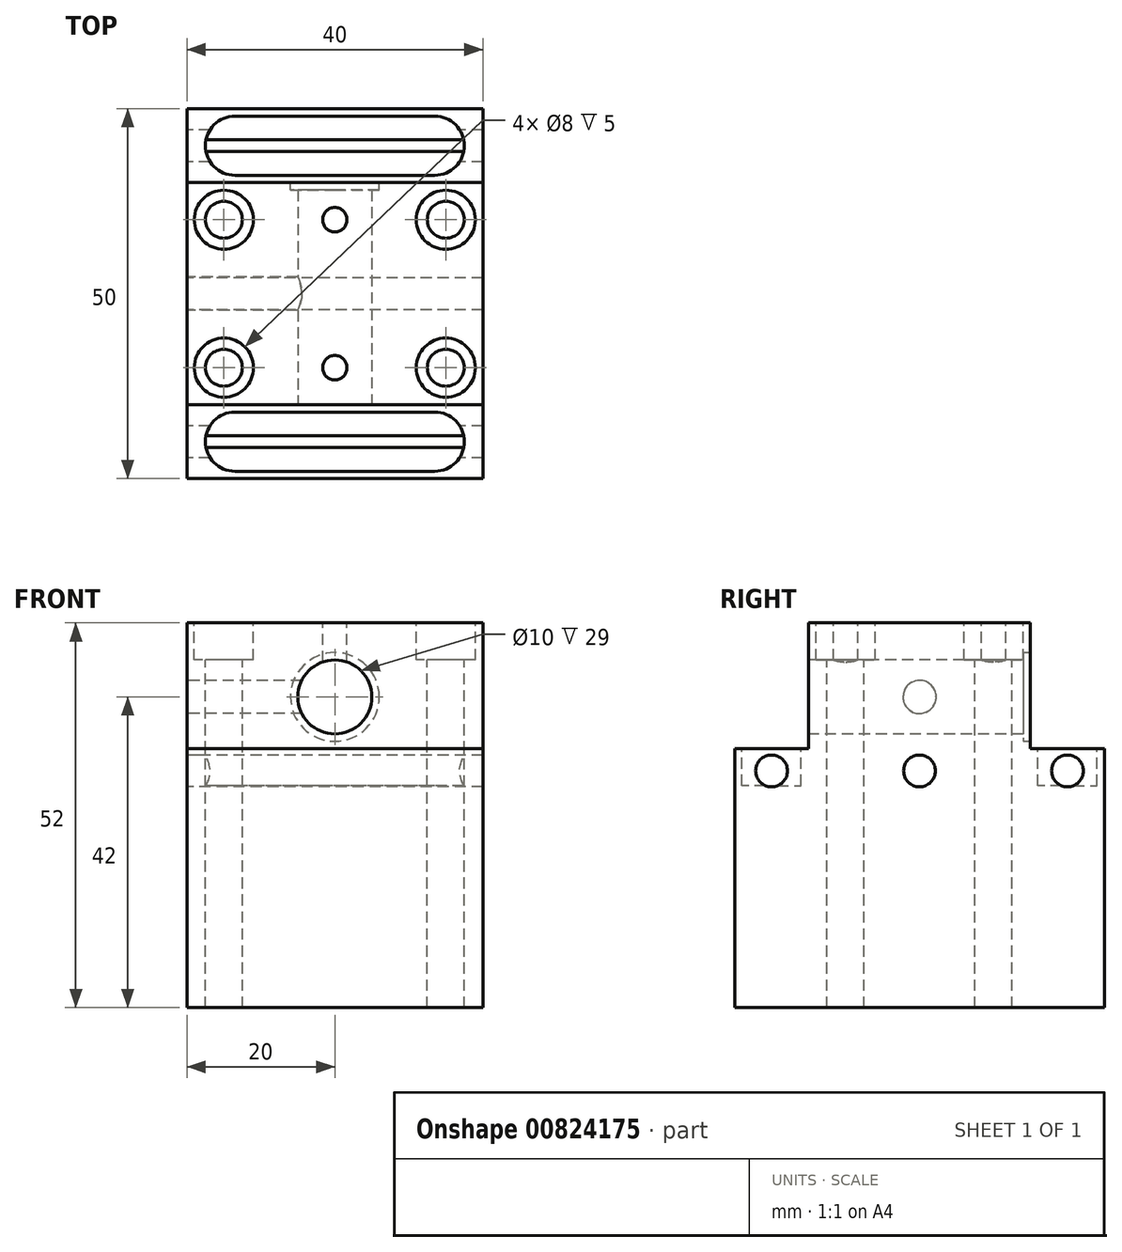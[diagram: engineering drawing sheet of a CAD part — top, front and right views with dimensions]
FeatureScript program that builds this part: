
annotation { "Feature Type Name" : "Feature", "Feature Type Description" : "" }
export const myFeature = defineFeature(function(context is Context, id is Id, definition is map)
    precondition{}
    {
        {
            var Q0;
            Q0=qCreatedBy(makeId("Top.planeOp"),FACE);
            var sketch = newSketch(context, id + "F0", { "sketchPlane" : qUnion([Q0])});
            skLineSegment(sketch, "E0.bottom", {"start": v(0, 0) * mm, "end": v(40, 0) * mm});
            skLineSegment(sketch, "E0.top", {"start": v(0, 30) * mm, "end": v(40, 30) * mm});
            skLineSegment(sketch, "E0.left", {"start": v(0, 0) * mm, "end": v(0, 30) * mm});
            skLineSegment(sketch, "E0.right", {"start": v(40, 0) * mm, "end": v(40, 30) * mm});
            skSolve(sketch);
        }
        {
            var Q0;
            Q0 = qSketchRegion(id + "F0", true);
            extrude(context, id + "F1", {"entities" : qUnion([Q0]), "depth" : 52 * mm, "offsetDistance" : 25 * mm});
        }
        {
            var Q0;
            Q0=makeQuery(id+"F1.opExtrude","SWEPT_FACE",FACE,{"disambiguationData":[OSD([sQuery(id+"F0.wireOp",EDGE,"E0.bottom")])]});
            var sketch = newSketch(context, id + "F2", { "sketchPlane" : qUnion([Q0])});
            skLineSegment(sketch, "E1", {"start": v(0, 42) * mm, "end": v(40, 42) * mm, "construction": true});
            skCircle(sketch, "E2", {"center": v(20, 42) * mm, "radius": 5 * mm});
            skSolve(sketch);
        }
        {
            var Q0;
            Q0 = qSketchRegion(id + "F2", true);
            extrude(context, id + "F3", {"entities" : qUnion([Q0]), "operationType" : NewBodyOperationType.REMOVE, "oppositeDirection" : true, "depth" : 20 * mm, "offsetDistance" : 25 * mm});
        }
        {
            var Q0;
            Q0=makeQuery(id+"F1.opExtrude","CAP_FACE",FACE,{"disambiguationData":[OSD([sQuery(id+"F0.wireOp",EDGE,"E0.bottom"),sQuery(id+"F0.wireOp",EDGE,"E0.top"),sQuery(id+"F0.wireOp",EDGE,"E0.left"),sQuery(id+"F0.wireOp",EDGE,"E0.right")])],"isStart":false});
            var sketch = newSketch(context, id + "F4", { "sketchPlane" : qUnion([Q0])});
            skLineSegment(sketch, "E3", {"start": v(0, 5) * mm, "end": v(40, 5) * mm, "construction": true});
            skLineSegment(sketch, "E4", {"start": v(0, 25) * mm, "end": v(40, 25) * mm, "construction": true});
            skCircle(sketch, "E5", {"center": v(20, 5) * mm, "radius": 1.65 * mm});
            skCircle(sketch, "E6", {"center": v(20, 25) * mm, "radius": 1.65 * mm});
            skLineSegment(sketch, "E7", {"start": v(0, 15) * mm, "end": v(40, 15) * mm, "construction": true});
            skSolve(sketch);
        }
        {
            var Q0;
            Q0 = qSketchRegion(id + "F4", true);
            extrude(context, id + "F5", {"entities" : qUnion([Q0]), "operationType" : NewBodyOperationType.REMOVE, "oppositeDirection" : true, "depth" : 10 * mm, "offsetDistance" : 25 * mm});
        }
        {
            var Q0;
            Q0=makeQuery(id+"F1.opExtrude","CAP_FACE",FACE,{"disambiguationData":[OSD([sQuery(id+"F0.wireOp",EDGE,"E0.bottom"),sQuery(id+"F0.wireOp",EDGE,"E0.top"),sQuery(id+"F0.wireOp",EDGE,"E0.left"),sQuery(id+"F0.wireOp",EDGE,"E0.right")])],"isStart":false});
            var sketch = newSketch(context, id + "F6", { "sketchPlane" : qUnion([Q0])});
            skLineSegment(sketch, "E8", {"start": v(0, 5) * mm, "end": v(40, 5) * mm, "construction": true});
            skCircle(sketch, "E9", {"center": v(5, 5) * mm, "radius": 2.5 * mm});
            skCircle(sketch, "E10.0.1.0", {"center": v(5, 25) * mm, "radius": 2.5 * mm});
            skCircle(sketch, "E10.1.0.0", {"center": v(35, 5) * mm, "radius": 2.5 * mm});
            skCircle(sketch, "E10.1.1.0", {"center": v(35, 25) * mm, "radius": 2.5 * mm});
            skLineSegment(sketch, "E10.direction1", {"start": v(5, 5) * mm, "end": v(35, 5) * mm, "construction": true});
            skLineSegment(sketch, "E10.direction2", {"start": v(5, 5) * mm, "end": v(5, 25) * mm, "construction": true});
            skSolve(sketch);
        }
        {
            var Q0;
            Q0 = qSketchRegion(id + "F6", true);
            extrude(context, id + "F7", {"entities" : qUnion([Q0]), "operationType" : NewBodyOperationType.REMOVE, "endBound" : BoundingType.THROUGH_ALL, "oppositeDirection" : true, "depth" : 25 * mm, "offsetDistance" : 25 * mm});
        }
        {
            var Q0;
            Q0=makeQuery(id+"F1.opExtrude","CAP_FACE",FACE,{"disambiguationData":[OSD([sQuery(id+"F0.wireOp",EDGE,"E0.bottom"),sQuery(id+"F0.wireOp",EDGE,"E0.top"),sQuery(id+"F0.wireOp",EDGE,"E0.left"),sQuery(id+"F0.wireOp",EDGE,"E0.right")])],"isStart":false});
            var sketch = newSketch(context, id + "F8", { "sketchPlane" : qUnion([Q0])});
            skCircle(sketch, "E11", {"center": v(5, 25) * mm, "radius": 4 * mm});
            skCircle(sketch, "E12.0.1.0", {"center": v(5, 5) * mm, "radius": 4 * mm});
            skCircle(sketch, "E12.1.0.0", {"center": v(35, 25) * mm, "radius": 4 * mm});
            skCircle(sketch, "E12.1.1.0", {"center": v(35, 5) * mm, "radius": 4 * mm});
            skLineSegment(sketch, "E12.direction1", {"start": v(5, 25) * mm, "end": v(35, 25) * mm, "construction": true});
            skLineSegment(sketch, "E12.direction2", {"start": v(5, 25) * mm, "end": v(5, 5) * mm, "construction": true});
            skSolve(sketch);
        }
        {
            var Q0;
            Q0 = qSketchRegion(id + "F8", true);
            extrude(context, id + "F9", {"entities" : qUnion([Q0]), "operationType" : NewBodyOperationType.REMOVE, "oppositeDirection" : true, "depth" : 5 * mm, "offsetDistance" : 25 * mm});
        }
        {
            var Q0;
            Q0=makeQuery(id+"F1.opExtrude","SWEPT_FACE",FACE,{"disambiguationData":[OSD([sQuery(id+"F0.wireOp",EDGE,"E0.bottom")])]});
            var sketch = newSketch(context, id + "F10", { "sketchPlane" : qUnion([Q0])});
            skLineSegment(sketch, "E13.bottom", {"start": v(0, 0) * mm, "end": v(40, 0) * mm});
            skLineSegment(sketch, "E13.top", {"start": v(0, 35) * mm, "end": v(40, 35) * mm});
            skLineSegment(sketch, "E13.left", {"start": v(0, 0) * mm, "end": v(0, 35) * mm});
            skLineSegment(sketch, "E13.right", {"start": v(40, 0) * mm, "end": v(40, 35) * mm});
            skSolve(sketch);
        }
        {
            var Q0;
            Q0 = qSketchRegion(id + "F10", true);
            extrude(context, id + "F11", {"entities" : qUnion([Q0]), "operationType" : NewBodyOperationType.ADD, "depth" : 10 * mm, "offsetDistance" : 25 * mm});
        }
        {
            var Q0;
            Q0=makeQuery(id+"F1.opExtrude","SWEPT_FACE",FACE,{"disambiguationData":[OSD([sQuery(id+"F0.wireOp",EDGE,"E0.top")])]});
            var sketch = newSketch(context, id + "F12", { "sketchPlane" : qUnion([Q0])});
            skLineSegment(sketch, "E14.bottom", {"start": v(-40, 0) * mm, "end": v(0, 0) * mm});
            skLineSegment(sketch, "E14.top", {"start": v(-40, 35) * mm, "end": v(0, 35) * mm});
            skLineSegment(sketch, "E14.left", {"start": v(-40, 0) * mm, "end": v(-40, 35) * mm});
            skLineSegment(sketch, "E14.right", {"start": v(0, 0) * mm, "end": v(0, 35) * mm});
            skSolve(sketch);
        }
        {
            var Q0;
            Q0 = qSketchRegion(id + "F12", true);
            extrude(context, id + "F13", {"entities" : qUnion([Q0]), "operationType" : NewBodyOperationType.ADD, "depth" : 10 * mm, "offsetDistance" : 25 * mm});
        }
        {
            var Q0;
            Q0=makeQuery(id+"F13.opExtrude","SWEPT_FACE",FACE,{"disambiguationData":[OSD([sQuery(id+"F12.wireOp",EDGE,"E14.top")])]});
            var sketch = newSketch(context, id + "F14", { "sketchPlane" : qUnion([Q0])});
            skLineSegment(sketch, "E15.bottom", {"start": v(33.5, 31) * mm, "end": v(6.5, 31) * mm});
            skLineSegment(sketch, "E15.top", {"start": v(33.5, 39) * mm, "end": v(6.5, 39) * mm});
            skLineSegment(sketch, "E15.left", {"start": v(37.5, 35) * mm, "end": v(37.5, 35) * mm});
            skLineSegment(sketch, "E15.right", {"start": v(2.5, 35) * mm, "end": v(2.5, 35) * mm});
            skLineSegment(sketch, "E16", {"start": v(40, 15) * mm, "end": v(0, 15) * mm, "construction": true});
            skPoint(sketch, "E17.visualSharp", {"position": v(37.5, 31) * mm});
            skArc(sketch, "E17.filletArc", {"start": v(33.5, 31) * mm, "mid": v(36.33, 32.17) * mm, "end": v(37.5, 35) * mm});
            skPoint(sketch, "E18.visualSharp", {"position": v(2.5, 31) * mm});
            skArc(sketch, "E18.filletArc", {"start": v(2.5, 35) * mm, "mid": v(3.67, 32.17) * mm, "end": v(6.5, 31) * mm});
            skPoint(sketch, "E19.visualSharp", {"position": v(2.5, 39) * mm});
            skArc(sketch, "E19.filletArc", {"start": v(6.5, 39) * mm, "mid": v(3.67, 37.83) * mm, "end": v(2.5, 35) * mm});
            skPoint(sketch, "E20.visualSharp", {"position": v(37.5, 39) * mm});
            skArc(sketch, "E20.filletArc", {"start": v(37.5, 35) * mm, "mid": v(36.33, 37.83) * mm, "end": v(33.5, 39) * mm});
            skPoint(sketch, "E21.MirrorP", {"position": v(37.5, -1) * mm});
            skPoint(sketch, "E22.MirrorP", {"position": v(2.5, -1) * mm});
            skLineSegment(sketch, "E23.MirrorCS", {"start": v(33.5, -9) * mm, "end": v(6.5, -9) * mm});
            skPoint(sketch, "E24.MirrorP", {"position": v(2.5, -9) * mm});
            skPoint(sketch, "E25.MirrorP", {"position": v(37.5, -9) * mm});
            skLineSegment(sketch, "E26.MirrorCS", {"start": v(33.5, -1) * mm, "end": v(6.5, -1) * mm});
            skArc(sketch, "E27.MirrorCS", {"start": v(2.5, -5) * mm, "mid": v(3.67, -2.17) * mm, "end": v(6.5, -1) * mm});
            skArc(sketch, "E28.MirrorCS", {"start": v(6.5, -9) * mm, "mid": v(3.67, -7.83) * mm, "end": v(2.5, -5) * mm});
            skLineSegment(sketch, "E29.MirrorCS", {"start": v(2.5, -5) * mm, "end": v(2.5, -5) * mm});
            skArc(sketch, "E30.MirrorCS", {"start": v(33.5, -1) * mm, "mid": v(36.33, -2.17) * mm, "end": v(37.5, -5) * mm});
            skArc(sketch, "E31.MirrorCS", {"start": v(37.5, -5) * mm, "mid": v(36.33, -7.83) * mm, "end": v(33.5, -9) * mm});
            skLineSegment(sketch, "E32.MirrorCS", {"start": v(37.5, -5) * mm, "end": v(37.5, -5) * mm});
            skSolve(sketch);
        }
        {
            var Q0;
            Q0 = qSketchRegion(id + "F14", true);
            extrude(context, id + "F15", {"entities" : qUnion([Q0]), "operationType" : NewBodyOperationType.REMOVE, "oppositeDirection" : true, "depth" : 5 * mm, "offsetDistance" : 25 * mm});
        }
        {
            var Q0;
            Q0=makeQuery(id+"F13.boolean.opBoolean","MERGE",FACE,{"derivedFrom":[makeQuery(id+"F11.boolean.opBoolean","MERGE",FACE,{"derivedFrom":[makeQuery(id+"F1.opExtrude","SWEPT_FACE",FACE,{"disambiguationData":[OSD([sQuery(id+"F0.wireOp",EDGE,"E0.left")])]}),makeQuery(id+"F11.opExtrude","SWEPT_FACE",FACE,{"disambiguationData":[OSD([sQuery(id+"F10.wireOp",EDGE,"E13.left")])]})]}),makeQuery(id+"F13.opExtrude","SWEPT_FACE",FACE,{"disambiguationData":[OSD([sQuery(id+"F12.wireOp",EDGE,"E14.right")])]})]});
            var sketch = newSketch(context, id + "F16", { "sketchPlane" : qUnion([Q0])});
            skLineSegment(sketch, "E33", {"start": v(-15, 52) * mm, "end": v(-15, 0) * mm, "construction": true});
            skCircle(sketch, "E34", {"center": v(-15, 32) * mm, "radius": 2.15 * mm});
            skLineSegment(sketch, "E35", {"start": v(-40, 32) * mm, "end": v(10, 32) * mm, "construction": true});
            skCircle(sketch, "E36", {"center": v(-35, 32) * mm, "radius": 2.15 * mm});
            skCircle(sketch, "E37", {"center": v(5, 32) * mm, "radius": 2.15 * mm});
            skSolve(sketch);
        }
        {
            var Q0;
            Q0 = qSketchRegion(id + "F16", true);
            extrude(context, id + "F17", {"entities" : qUnion([Q0]), "operationType" : NewBodyOperationType.REMOVE, "endBound" : BoundingType.THROUGH_ALL, "oppositeDirection" : true, "depth" : 25 * mm, "offsetDistance" : 25 * mm});
        }
        {
            var Q0;
            Q0=makeQuery(id+"F1.opExtrude","SWEPT_FACE",FACE,{"disambiguationData":[OSD([sQuery(id+"F0.wireOp",EDGE,"E0.top")])]});
            var sketch = newSketch(context, id + "F18", { "sketchPlane" : qUnion([Q0])});
            skLineSegment(sketch, "E38", {"start": v(0, 42) * mm, "end": v(-40, 42) * mm, "construction": true});
            skCircle(sketch, "E39", {"center": v(-20, 42) * mm, "radius": 5 * mm});
            skSolve(sketch);
        }
        {
            var Q0;
            Q0 = qSketchRegion(id + "F18", true);
            extrude(context, id + "F19", {"entities" : qUnion([Q0]), "operationType" : NewBodyOperationType.REMOVE, "endBound" : BoundingType.THROUGH_ALL, "oppositeDirection" : true, "depth" : 15 * mm, "offsetDistance" : 25 * mm});
        }
        {
            var Q0;
            Q0=makeQuery(id+"F1.opExtrude","SWEPT_FACE",FACE,{"disambiguationData":[OSD([sQuery(id+"F0.wireOp",EDGE,"E0.top")])]});
            var sketch = newSketch(context, id + "F20", { "sketchPlane" : qUnion([Q0])});
            skCircle(sketch, "E40", {"center": v(-20, 42) * mm, "radius": 6 * mm});
            skSolve(sketch);
        }
        {
            var Q0;
            Q0 = qSketchRegion(id + "F20", true);
            extrude(context, id + "F21", {"entities" : qUnion([Q0]), "operationType" : NewBodyOperationType.REMOVE, "oppositeDirection" : true, "depth" : 1 * mm, "offsetDistance" : 25 * mm});
        }
        {
            var Q0;
            Q0=makeQuery(id+"F13.boolean.opBoolean","MERGE",FACE,{"derivedFrom":[makeQuery(id+"F11.boolean.opBoolean","MERGE",FACE,{"derivedFrom":[makeQuery(id+"F1.opExtrude","SWEPT_FACE",FACE,{"disambiguationData":[OSD([sQuery(id+"F0.wireOp",EDGE,"E0.left")])]}),makeQuery(id+"F11.opExtrude","SWEPT_FACE",FACE,{"disambiguationData":[OSD([sQuery(id+"F10.wireOp",EDGE,"E13.left")])]})]}),makeQuery(id+"F13.opExtrude","SWEPT_FACE",FACE,{"disambiguationData":[OSD([sQuery(id+"F12.wireOp",EDGE,"E14.right")])]})]});
            var sketch = newSketch(context, id + "F22", { "sketchPlane" : qUnion([Q0])});
            skLineSegment(sketch, "E41", {"start": v(-15, 52) * mm, "end": v(-15, 17.99) * mm, "construction": true});
            skCircle(sketch, "E42", {"center": v(-15, 42) * mm, "radius": 2.25 * mm});
            skSolve(sketch);
        }
        {
            var Q0;
            Q0 = qSketchRegion(id + "F22", true);
            extrude(context, id + "F23", {"entities" : qUnion([Q0]), "operationType" : NewBodyOperationType.REMOVE, "endBound" : BoundingType.UP_TO_NEXT, "oppositeDirection" : true, "depth" : 25 * mm, "offsetDistance" : 25 * mm});
        }
    });
